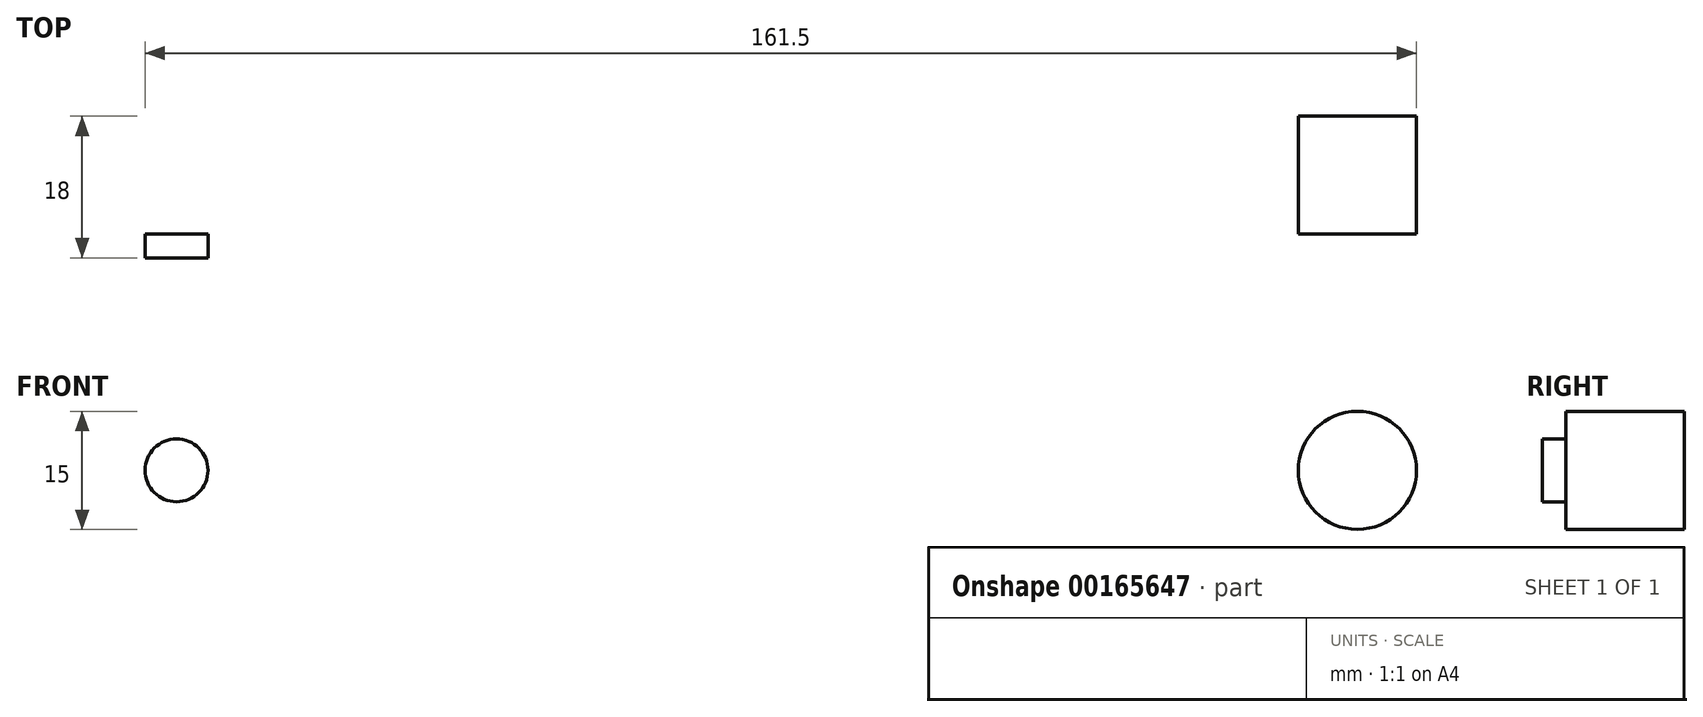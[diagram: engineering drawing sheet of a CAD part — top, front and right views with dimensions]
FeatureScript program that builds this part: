
annotation { "Feature Type Name" : "Feature", "Feature Type Description" : "" }
export const myFeature = defineFeature(function(context is Context, id is Id, definition is map)
    precondition{}
    {
        {
            var Q0;
            Q0=qCreatedBy(makeId("Top.planeOp"),FACE);
            var sketch = newSketch(context, id + "F0", { "sketchPlane" : qUnion([Q0])});
            skLineSegment(sketch, "E0.bottom", {"start": v(85, -1.5) * mm, "end": v(-85, -1.5) * mm});
            skLineSegment(sketch, "E0.top", {"start": v(85, 1.5) * mm, "end": v(-85, 1.5) * mm});
            skLineSegment(sketch, "E0.left", {"start": v(85, -1.5) * mm, "end": v(85, 1.5) * mm});
            skLineSegment(sketch, "E0.right", {"start": v(-85, -1.5) * mm, "end": v(-85, 1.5) * mm});
            skPoint(sketch, "E0.middle", {"position": v(0, 0) * mm});
            skSolve(sketch);
        }
        {
            var Q0;
            Q0=makeQuery(id+"F0.imprint","IMPRINT",FACE,{"disambiguationData":[TD([[makeQuery(id+"F0.imprint","IMPRINT",EDGE,{"derivedFrom":sQuery(id+"F0.wireOp",EDGE,"E0.bottom")}),-1.0]])]});
            extrude(context, id + "F1", {"entities" : qUnion([Q0]), "endBound" : BoundingType.SYMMETRIC, "depth" : 20 * mm, "offsetDistance" : 25 * mm});
        }
        {
            var Q0;
            Q0=makeQuery(id+"F1.opExtrude","CAP_EDGE",EDGE,{"disambiguationData":[OSD([sQuery(id+"F0.wireOp",EDGE,"E0.right")])],"isStart":false});
            var Q1;
            Q1=makeQuery(id+"F1.opExtrude","CAP_EDGE",EDGE,{"disambiguationData":[OSD([sQuery(id+"F0.wireOp",EDGE,"E0.right")])],"isStart":true});
            var Q2;
            Q2=makeQuery(id+"F1.opExtrude","CAP_EDGE",EDGE,{"disambiguationData":[OSD([sQuery(id+"F0.wireOp",EDGE,"E0.left")])],"isStart":false});
            var Q3;
            Q3=makeQuery(id+"F1.opExtrude","CAP_EDGE",EDGE,{"disambiguationData":[OSD([sQuery(id+"F0.wireOp",EDGE,"E0.left")])],"isStart":true});
            fillet(context, id + "F2", {"entities" : qUnion([Q0, Q1, Q2, Q3]), "radius" : 10 * mm, "tangentPropagation" : true});
        }
        {
            var Q0;
            Q0=makeQuery(id+"F1.opExtrude","SWEPT_FACE",FACE,{"disambiguationData":[OSD([sQuery(id+"F0.wireOp",EDGE,"E0.top")])]});
            var sketch = newSketch(context, id + "F3", { "sketchPlane" : qUnion([Q0])});
            skCircle(sketch, "E1", {"center": v(-75, 0) * mm, "radius": 4 * mm});
            skCircle(sketch, "E2.MirrorC", {"center": v(75, 0) * mm, "radius": 4 * mm});
            skSolve(sketch);
        }
        {
            var Q0;
            Q0=makeQuery(id+"F3.imprint","IMPRINT",FACE,{"disambiguationData":[TD([[makeQuery(id+"F3.imprint","IMPRINT",EDGE,{"derivedFrom":sQuery(id+"F3.wireOp",EDGE,"E1")}),1.0]])]});
            var Q1;
            Q1=makeQuery(id+"F3.imprint","IMPRINT",FACE,{"disambiguationData":[TD([[makeQuery(id+"F3.imprint","IMPRINT",EDGE,{"derivedFrom":sQuery(id+"F3.wireOp",EDGE,"E2.MirrorC")}),-1.0]])]});
            extrude(context, id + "F4", {"entities" : qUnion([Q0, Q1]), "operationType" : NewBodyOperationType.REMOVE, "endBound" : BoundingType.UP_TO_NEXT, "oppositeDirection" : true, "depth" : 25 * mm, "offsetDistance" : 25 * mm});
        }
        {
            var Q0;
            Q0=makeQuery(id+"F1.opExtrude","SWEPT_FACE",FACE,{"disambiguationData":[OSD([sQuery(id+"F0.wireOp",EDGE,"E0.top")])]});
            var sketch = newSketch(context, id + "F5", { "sketchPlane" : qUnion([Q0])});
            skCircle(sketch, "E3", {"center": v(-75, 0) * mm, "radius": 7.5 * mm});
            skSolve(sketch);
        }
        {
            var Q0;
            Q0=makeQuery(id+"F5.imprint","IMPRINT",FACE,{"disambiguationData":[TD([[makeQuery(id+"F5.imprint","IMPRINT",EDGE,{"derivedFrom":sQuery(id+"F5.wireOp",EDGE,"E3")}),1.0]])]});
            extrude(context, id + "F6", {"entities" : qUnion([Q0]), "depth" : 15 * mm, "offsetDistance" : 25 * mm});
        }
    });
